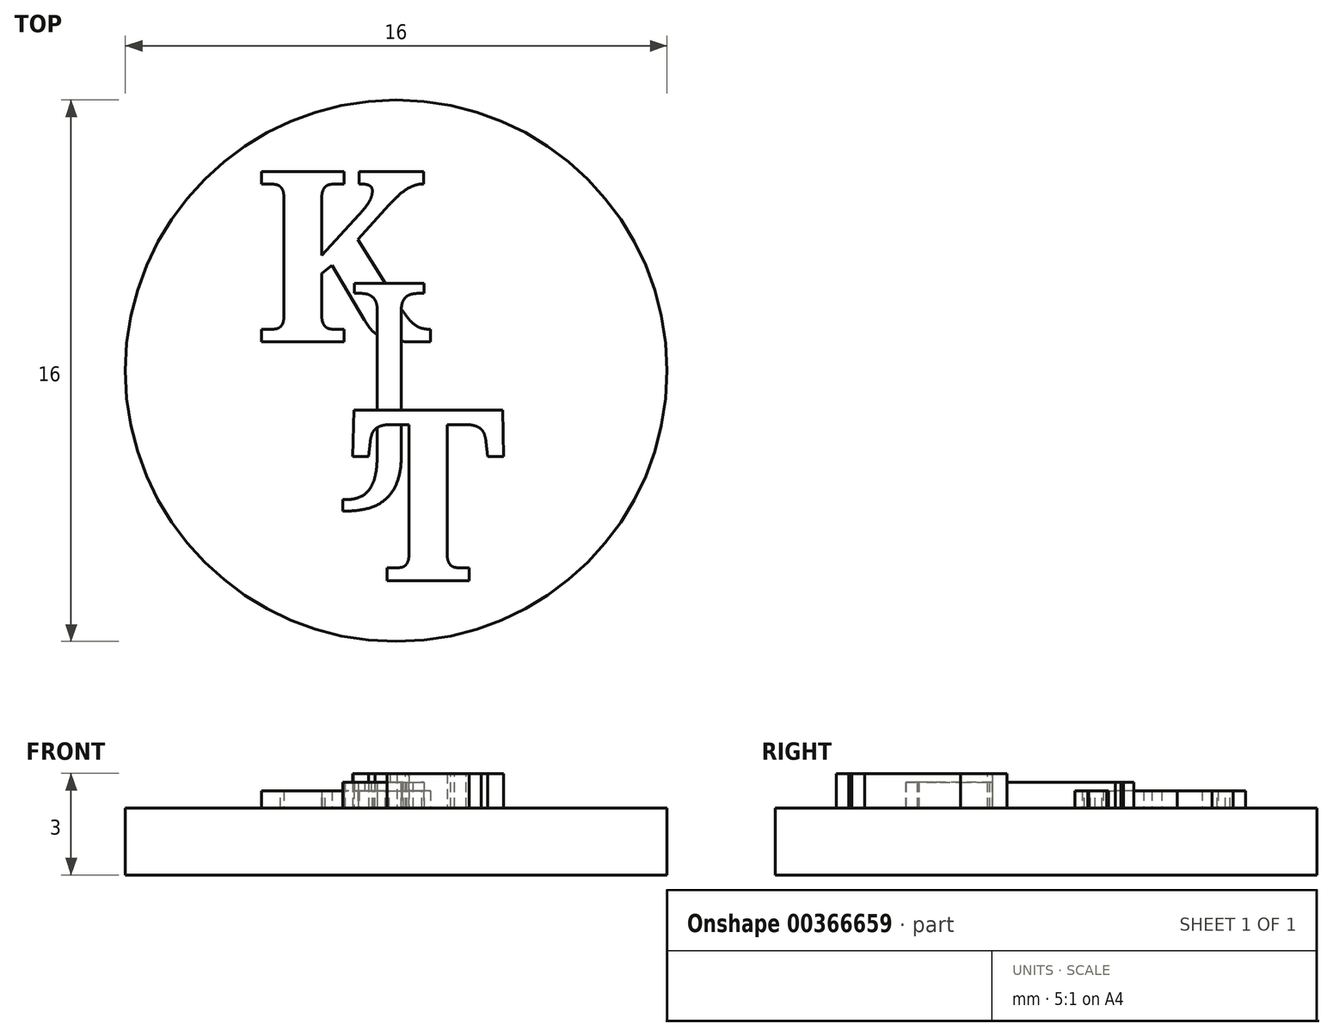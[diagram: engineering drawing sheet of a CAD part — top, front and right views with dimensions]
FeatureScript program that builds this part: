
annotation { "Feature Type Name" : "Feature", "Feature Type Description" : "" }
export const myFeature = defineFeature(function(context is Context, id is Id, definition is map)
    precondition{}
    {
        {
            var Q0;
            Q0=qCreatedBy(makeId("Top.planeOp"),FACE);
            var sketch = newSketch(context, id + "F0", { "sketchPlane" : qUnion([Q0])});
            skCircle(sketch, "E0", {"center": v(0, 0) * mm, "radius": 8 * mm});
            skSolve(sketch);
        }
        {
            var Q0;
            Q0=qSketchRegion(id+"F0",true);
            extrude(context, id + "F1", {"entities" : qUnion([Q0]), "depth" : 1.98 * mm});
        }
        {
            var Q0;
            Q0=makeQuery(id+"F1.opExtrude","CAP_FACE",FACE,{"disambiguationData":[OSD([sQuery(id+"F0.wireOp",EDGE,"E0")])],"isStart":false});
            var sketch = newSketch(context, id + "F2", { "sketchPlane" : qUnion([Q0])});
            skText(sketch, "E1", { "text": "K", "fontName": "NotoSerif-Bold.ttf"});
            const initialGuessF2  = {"E1": [-0.00417, 0.00085, 1, 0, 0.00508]};
            skSetInitialGuess(sketch, initialGuessF2);
            skSolve(sketch);
        }
        {
            var Q0;
            Q0=makeQuery(id+"F2.imprint","IMPRINT",FACE,{"disambiguationData":[TD([[makeQuery(id+"F2.imprint","IMPRINT",EDGE,{"derivedFrom":sQuery(id+"F2.wireOp",EDGE,"E1.sketch_text.stroke-0")}),1.0]])]});
            var sketch = newSketch(context, id + "F3", { "sketchPlane" : qUnion([Q0])});
            skText(sketch, "E2", { "text": "J", "fontName": "NotoSerif-Regular.ttf"});
            const initialGuessF3  = {"E2": [-0.0015, -0.00245, 1, 0, 0.00508]};
            skSetInitialGuess(sketch, initialGuessF3);
            skSolve(sketch);
        }
        {
            var Q0;
            Q0=makeQuery(id+"F2.imprint","IMPRINT",FACE,{"disambiguationData":[TD([[makeQuery(id+"F2.imprint","IMPRINT",EDGE,{"derivedFrom":sQuery(id+"F2.wireOp",EDGE,"E1.sketch_text.stroke-0")}),1.0]])]});
            var sketch = newSketch(context, id + "F4", { "sketchPlane" : qUnion([Q0])});
            skText(sketch, "E3", { "text": "T", "fontName": "NotoSerif-Bold.ttf"});
            const initialGuessF4  = {"E3": [-0.00136, -0.0062, 1, 0, 0.00508]};
            skSetInitialGuess(sketch, initialGuessF4);
            skSolve(sketch);
        }
        {
            var Q0;
            Q0=qSketchRegion(id+"F2",true);
            extrude(context, id + "F5", {"entities" : qUnion([Q0]), "operationType" : NewBodyOperationType.ADD, "depth" : 0.5 * mm});
        }
        {
            var Q0;
            Q0=qSketchRegion(id+"F3",true);
            extrude(context, id + "F6", {"entities" : qUnion([Q0]), "operationType" : NewBodyOperationType.ADD, "depth" : 0.76 * mm});
        }
        {
            var Q0;
            Q0=qSketchRegion(id+"F4",true);
            extrude(context, id + "F7", {"entities" : qUnion([Q0]), "operationType" : NewBodyOperationType.ADD, "depth" : 1.02 * mm});
        }
    });
